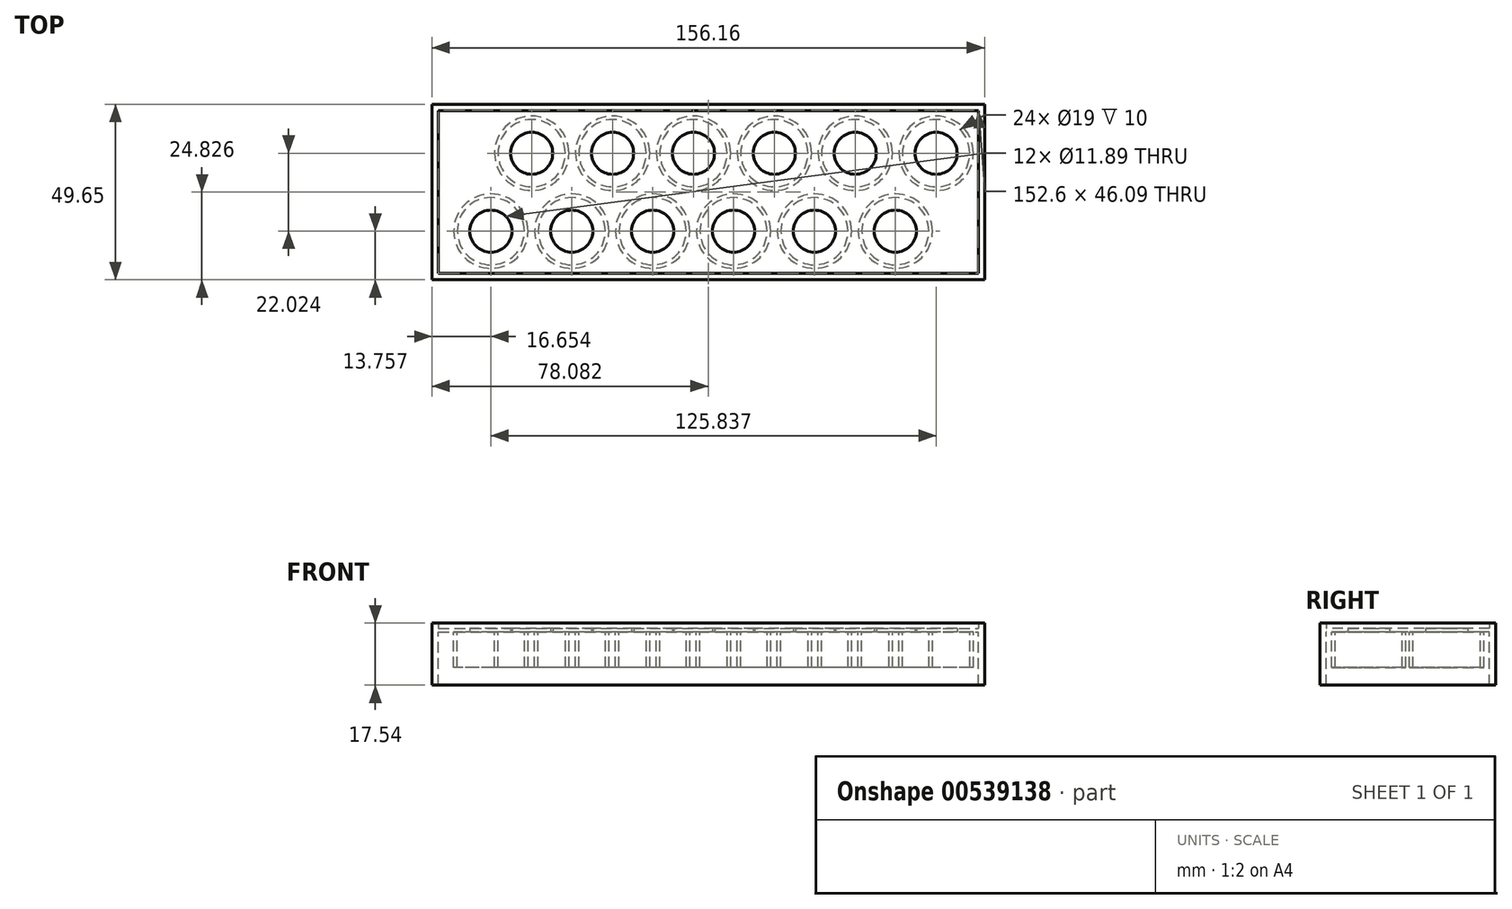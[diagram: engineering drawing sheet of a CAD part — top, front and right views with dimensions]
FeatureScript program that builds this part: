
annotation { "Feature Type Name" : "Feature", "Feature Type Description" : "" }
export const myFeature = defineFeature(function(context is Context, id is Id, definition is map)
    precondition{}
    {
        {
            var Q0;
            Q0=qCreatedBy(makeId("Top.planeOp"),FACE);
            var sketch = newSketch(context, id + "F0", { "sketchPlane" : qUnion([Q0])});
            skCircle(sketch, "E0", {"center": v(-57.63, 20.67) * mm, "radius": 9.5 * mm});
            skCircle(sketch, "E1.0", {"center": v(-57.63, 20.67) * mm, "radius": 10.52 * mm});
            skCircle(sketch, "E2.0.1.0", {"center": v(-46.09, 42.7) * mm, "radius": 10.52 * mm});
            skCircle(sketch, "E2.0.1.1", {"center": v(-46.09, 42.7) * mm, "radius": 9.5 * mm});
            skCircle(sketch, "E2.1.0.0", {"center": v(-34.77, 20.67) * mm, "radius": 10.52 * mm});
            skCircle(sketch, "E2.1.0.1", {"center": v(-34.77, 20.67) * mm, "radius": 9.5 * mm});
            skCircle(sketch, "E2.1.1.0", {"center": v(-23.23, 42.7) * mm, "radius": 10.52 * mm});
            skCircle(sketch, "E2.1.1.1", {"center": v(-23.23, 42.7) * mm, "radius": 9.5 * mm});
            skCircle(sketch, "E2.2.0.0", {"center": v(-11.9, 20.67) * mm, "radius": 10.52 * mm});
            skCircle(sketch, "E2.2.0.1", {"center": v(-11.9, 20.67) * mm, "radius": 9.5 * mm});
            skCircle(sketch, "E2.2.1.0", {"center": v(-0.37, 42.7) * mm, "radius": 10.52 * mm});
            skCircle(sketch, "E2.2.1.1", {"center": v(-0.37, 42.7) * mm, "radius": 9.5 * mm});
            skCircle(sketch, "E2.3.0.0", {"center": v(10.95, 20.67) * mm, "radius": 10.52 * mm});
            skCircle(sketch, "E2.3.0.1", {"center": v(10.95, 20.67) * mm, "radius": 9.5 * mm});
            skCircle(sketch, "E2.3.1.0", {"center": v(22.5, 42.7) * mm, "radius": 10.52 * mm});
            skCircle(sketch, "E2.3.1.1", {"center": v(22.5, 42.7) * mm, "radius": 9.5 * mm});
            skCircle(sketch, "E2.4.0.0", {"center": v(33.81, 20.67) * mm, "radius": 10.52 * mm});
            skCircle(sketch, "E2.4.0.1", {"center": v(33.81, 20.67) * mm, "radius": 9.5 * mm});
            skCircle(sketch, "E2.4.1.0", {"center": v(45.35, 42.7) * mm, "radius": 10.52 * mm});
            skCircle(sketch, "E2.4.1.1", {"center": v(45.35, 42.7) * mm, "radius": 9.5 * mm});
            skCircle(sketch, "E2.5.0.0", {"center": v(56.67, 20.67) * mm, "radius": 10.52 * mm});
            skCircle(sketch, "E2.5.0.1", {"center": v(56.67, 20.67) * mm, "radius": 9.5 * mm});
            skCircle(sketch, "E2.5.1.0", {"center": v(68.21, 42.7) * mm, "radius": 10.52 * mm});
            skCircle(sketch, "E2.5.1.1", {"center": v(68.21, 42.7) * mm, "radius": 9.5 * mm});
            skLineSegment(sketch, "E2.direction1", {"start": v(-57.63, 20.67) * mm, "end": v(-34.77, 20.67) * mm, "construction": true});
            skLineSegment(sketch, "E2.direction2", {"start": v(-57.63, 20.67) * mm, "end": v(-46.09, 42.7) * mm, "construction": true});
            skLineSegment(sketch, "E3.bottom", {"start": v(-74.28, 56.56) * mm, "end": v(81.88, 56.56) * mm});
            skLineSegment(sketch, "E3.top", {"start": v(-74.28, 6.91) * mm, "end": v(81.88, 6.91) * mm});
            skLineSegment(sketch, "E3.left", {"start": v(-74.28, 56.56) * mm, "end": v(-74.28, 6.91) * mm});
            skLineSegment(sketch, "E3.right", {"start": v(81.88, 56.56) * mm, "end": v(81.88, 6.91) * mm});
            skLineSegment(sketch, "E4.0", {"start": v(-72.5, 54.78) * mm, "end": v(80.1, 54.78) * mm});
            skLineSegment(sketch, "E4.1", {"start": v(-72.5, 54.78) * mm, "end": v(-72.5, 8.7) * mm});
            skLineSegment(sketch, "E4.2", {"start": v(-72.5, 8.7) * mm, "end": v(80.1, 8.7) * mm});
            skLineSegment(sketch, "E4.3", {"start": v(80.1, 54.78) * mm, "end": v(80.1, 8.7) * mm});
            skCircle(sketch, "E5.0", {"center": v(-57.63, 20.67) * mm, "radius": 5.94 * mm});
            skCircle(sketch, "E6.0", {"center": v(-46.09, 42.7) * mm, "radius": 5.94 * mm});
            skCircle(sketch, "E7.0", {"center": v(-23.23, 42.7) * mm, "radius": 5.94 * mm});
            skCircle(sketch, "E8.0", {"center": v(-34.77, 20.67) * mm, "radius": 5.94 * mm});
            skCircle(sketch, "E9.0", {"center": v(-0.37, 42.7) * mm, "radius": 5.94 * mm});
            skCircle(sketch, "E10.0", {"center": v(-11.9, 20.67) * mm, "radius": 5.94 * mm});
            skCircle(sketch, "E11.0", {"center": v(10.95, 20.67) * mm, "radius": 5.94 * mm});
            skCircle(sketch, "E12.0", {"center": v(22.5, 42.7) * mm, "radius": 5.94 * mm});
            skCircle(sketch, "E13.0", {"center": v(33.81, 20.67) * mm, "radius": 5.94 * mm});
            skCircle(sketch, "E14.0", {"center": v(45.35, 42.7) * mm, "radius": 5.94 * mm});
            skCircle(sketch, "E15.0", {"center": v(56.67, 20.67) * mm, "radius": 5.94 * mm});
            skCircle(sketch, "E16.0", {"center": v(68.21, 42.7) * mm, "radius": 5.94 * mm});
            skSolve(sketch);
        }
        {
            var Q0;
            Q0=makeQuery(id+"F0.imprint","IMPRINT",FACE,{"disambiguationData":[TD([[makeQuery(id+"F0.imprint","IMPRINT",EDGE,{"derivedFrom":sQuery(id+"F0.wireOp",EDGE,"E3.bottom")}),-1.0]])]});
            extrude(context, id + "F1", {"entities" : qUnion([Q0]), "depth" : 2.54 * mm, "offsetDistance" : 25.4 * mm});
        }
        {
            var Q0;
            Q0=makeQuery(id+"F0.imprint","IMPRINT",FACE,{"disambiguationData":[TD([[makeQuery(id+"F0.imprint","IMPRINT",EDGE,{"derivedFrom":sQuery(id+"F0.wireOp",EDGE,"E2.0.1.0")}),1.0]])]});
            var Q1;
            Q1=makeQuery(id+"F0.imprint","IMPRINT",FACE,{"disambiguationData":[TD([[makeQuery(id+"F0.imprint","IMPRINT",EDGE,{"derivedFrom":sQuery(id+"F0.wireOp",EDGE,"E0")}),-1.0]])]});
            var Q2;
            Q2=makeQuery(id+"F0.imprint","IMPRINT",FACE,{"disambiguationData":[TD([[makeQuery(id+"F0.imprint","IMPRINT",EDGE,{"derivedFrom":sQuery(id+"F0.wireOp",EDGE,"E2.1.0.0")}),1.0]])]});
            var Q3;
            Q3=makeQuery(id+"F0.imprint","IMPRINT",FACE,{"disambiguationData":[TD([[makeQuery(id+"F0.imprint","IMPRINT",EDGE,{"derivedFrom":sQuery(id+"F0.wireOp",EDGE,"E2.1.1.0")}),1.0]])]});
            var Q4;
            Q4=makeQuery(id+"F0.imprint","IMPRINT",FACE,{"disambiguationData":[TD([[makeQuery(id+"F0.imprint","IMPRINT",EDGE,{"derivedFrom":sQuery(id+"F0.wireOp",EDGE,"E2.2.1.0")}),1.0]])]});
            var Q5;
            Q5=makeQuery(id+"F0.imprint","IMPRINT",FACE,{"disambiguationData":[TD([[makeQuery(id+"F0.imprint","IMPRINT",EDGE,{"derivedFrom":sQuery(id+"F0.wireOp",EDGE,"E2.2.0.0")}),1.0]])]});
            var Q6;
            Q6=makeQuery(id+"F0.imprint","IMPRINT",FACE,{"disambiguationData":[TD([[makeQuery(id+"F0.imprint","IMPRINT",EDGE,{"derivedFrom":sQuery(id+"F0.wireOp",EDGE,"E2.3.0.0")}),1.0]])]});
            var Q7;
            Q7=makeQuery(id+"F0.imprint","IMPRINT",FACE,{"disambiguationData":[TD([[makeQuery(id+"F0.imprint","IMPRINT",EDGE,{"derivedFrom":sQuery(id+"F0.wireOp",EDGE,"E2.3.1.0")}),1.0]])]});
            var Q8;
            Q8=makeQuery(id+"F0.imprint","IMPRINT",FACE,{"disambiguationData":[TD([[makeQuery(id+"F0.imprint","IMPRINT",EDGE,{"derivedFrom":sQuery(id+"F0.wireOp",EDGE,"E2.4.0.0")}),1.0]])]});
            var Q9;
            Q9=makeQuery(id+"F0.imprint","IMPRINT",FACE,{"disambiguationData":[TD([[makeQuery(id+"F0.imprint","IMPRINT",EDGE,{"derivedFrom":sQuery(id+"F0.wireOp",EDGE,"E2.4.1.0")}),1.0]])]});
            var Q10;
            Q10=makeQuery(id+"F0.imprint","IMPRINT",FACE,{"disambiguationData":[TD([[makeQuery(id+"F0.imprint","IMPRINT",EDGE,{"derivedFrom":sQuery(id+"F0.wireOp",EDGE,"E2.5.0.0")}),1.0]])]});
            var Q11;
            Q11=makeQuery(id+"F0.imprint","IMPRINT",FACE,{"disambiguationData":[TD([[makeQuery(id+"F0.imprint","IMPRINT",EDGE,{"derivedFrom":sQuery(id+"F0.wireOp",EDGE,"E2.5.1.0")}),1.0]])]});
            extrude(context, id + "F2", {"entities" : qUnion([Q0, Q1, Q2, Q3, Q4, Q5, Q6, Q7, Q8, Q9, Q10, Q11]), "depth" : -10 * mm, "offsetDistance" : 25.4 * mm});
        }
        {
            var Q0;
            Q0=makeQuery(id+"F0.imprint","IMPRINT",FACE,{"disambiguationData":[TD([[makeQuery(id+"F0.imprint","IMPRINT",EDGE,{"derivedFrom":sQuery(id+"F0.wireOp",EDGE,"E1.0")}),-1.0]])]});
            var Q1;
            Q1=makeQuery(id+"F0.imprint","IMPRINT",FACE,{"disambiguationData":[TD([[makeQuery(id+"F0.imprint","IMPRINT",EDGE,{"derivedFrom":sQuery(id+"F0.wireOp",EDGE,"E2.0.1.1")}),1.0]])]});
            var Q2;
            Q2=makeQuery(id+"F0.imprint","IMPRINT",FACE,{"disambiguationData":[TD([[makeQuery(id+"F0.imprint","IMPRINT",EDGE,{"derivedFrom":sQuery(id+"F0.wireOp",EDGE,"E2.1.1.1")}),1.0]])]});
            var Q3;
            Q3=makeQuery(id+"F0.imprint","IMPRINT",FACE,{"disambiguationData":[TD([[makeQuery(id+"F0.imprint","IMPRINT",EDGE,{"derivedFrom":sQuery(id+"F0.wireOp",EDGE,"E0")}),1.0]])]});
            var Q4;
            Q4=makeQuery(id+"F0.imprint","IMPRINT",FACE,{"disambiguationData":[TD([[makeQuery(id+"F0.imprint","IMPRINT",EDGE,{"derivedFrom":sQuery(id+"F0.wireOp",EDGE,"E2.1.0.1")}),1.0]])]});
            var Q5;
            Q5=makeQuery(id+"F0.imprint","IMPRINT",FACE,{"disambiguationData":[TD([[makeQuery(id+"F0.imprint","IMPRINT",EDGE,{"derivedFrom":sQuery(id+"F0.wireOp",EDGE,"E2.2.0.1")}),1.0]])]});
            var Q6;
            Q6=makeQuery(id+"F0.imprint","IMPRINT",FACE,{"disambiguationData":[TD([[makeQuery(id+"F0.imprint","IMPRINT",EDGE,{"derivedFrom":sQuery(id+"F0.wireOp",EDGE,"E2.2.1.1")}),1.0]])]});
            var Q7;
            Q7=makeQuery(id+"F0.imprint","IMPRINT",FACE,{"disambiguationData":[TD([[makeQuery(id+"F0.imprint","IMPRINT",EDGE,{"derivedFrom":sQuery(id+"F0.wireOp",EDGE,"E2.3.1.1")}),1.0]])]});
            var Q8;
            Q8=makeQuery(id+"F0.imprint","IMPRINT",FACE,{"disambiguationData":[TD([[makeQuery(id+"F0.imprint","IMPRINT",EDGE,{"derivedFrom":sQuery(id+"F0.wireOp",EDGE,"E2.3.0.1")}),1.0]])]});
            var Q9;
            Q9=makeQuery(id+"F0.imprint","IMPRINT",FACE,{"disambiguationData":[TD([[makeQuery(id+"F0.imprint","IMPRINT",EDGE,{"derivedFrom":sQuery(id+"F0.wireOp",EDGE,"E2.4.0.1")}),1.0]])]});
            var Q10;
            Q10=makeQuery(id+"F0.imprint","IMPRINT",FACE,{"disambiguationData":[TD([[makeQuery(id+"F0.imprint","IMPRINT",EDGE,{"derivedFrom":sQuery(id+"F0.wireOp",EDGE,"E2.4.1.1")}),1.0]])]});
            var Q11;
            Q11=makeQuery(id+"F0.imprint","IMPRINT",FACE,{"disambiguationData":[TD([[makeQuery(id+"F0.imprint","IMPRINT",EDGE,{"derivedFrom":sQuery(id+"F0.wireOp",EDGE,"E2.5.0.1")}),1.0]])]});
            var Q12;
            Q12=makeQuery(id+"F0.imprint","IMPRINT",FACE,{"disambiguationData":[TD([[makeQuery(id+"F0.imprint","IMPRINT",EDGE,{"derivedFrom":sQuery(id+"F0.wireOp",EDGE,"E2.5.1.1")}),1.0]])]});
            var Q13;
            Q13=makeQuery(id+"F0.imprint","IMPRINT",FACE,{"disambiguationData":[TD([[makeQuery(id+"F0.imprint","IMPRINT",EDGE,{"derivedFrom":sQuery(id+"F0.wireOp",EDGE,"E2.0.1.0")}),1.0]])]});
            var Q14;
            Q14=makeQuery(id+"F0.imprint","IMPRINT",FACE,{"disambiguationData":[TD([[makeQuery(id+"F0.imprint","IMPRINT",EDGE,{"derivedFrom":sQuery(id+"F0.wireOp",EDGE,"E0")}),-1.0]])]});
            var Q15;
            Q15=makeQuery(id+"F0.imprint","IMPRINT",FACE,{"disambiguationData":[TD([[makeQuery(id+"F0.imprint","IMPRINT",EDGE,{"derivedFrom":sQuery(id+"F0.wireOp",EDGE,"E2.1.0.0")}),1.0]])]});
            var Q16;
            Q16=makeQuery(id+"F0.imprint","IMPRINT",FACE,{"disambiguationData":[TD([[makeQuery(id+"F0.imprint","IMPRINT",EDGE,{"derivedFrom":sQuery(id+"F0.wireOp",EDGE,"E2.1.1.0")}),1.0]])]});
            var Q17;
            Q17=makeQuery(id+"F0.imprint","IMPRINT",FACE,{"disambiguationData":[TD([[makeQuery(id+"F0.imprint","IMPRINT",EDGE,{"derivedFrom":sQuery(id+"F0.wireOp",EDGE,"E2.2.1.0")}),1.0]])]});
            var Q18;
            Q18=makeQuery(id+"F0.imprint","IMPRINT",FACE,{"disambiguationData":[TD([[makeQuery(id+"F0.imprint","IMPRINT",EDGE,{"derivedFrom":sQuery(id+"F0.wireOp",EDGE,"E2.3.0.0")}),1.0]])]});
            var Q19;
            Q19=makeQuery(id+"F0.imprint","IMPRINT",FACE,{"disambiguationData":[TD([[makeQuery(id+"F0.imprint","IMPRINT",EDGE,{"derivedFrom":sQuery(id+"F0.wireOp",EDGE,"E2.2.0.0")}),1.0]])]});
            var Q20;
            Q20=makeQuery(id+"F0.imprint","IMPRINT",FACE,{"disambiguationData":[TD([[makeQuery(id+"F0.imprint","IMPRINT",EDGE,{"derivedFrom":sQuery(id+"F0.wireOp",EDGE,"E2.5.0.0")}),1.0]])]});
            var Q21;
            Q21=makeQuery(id+"F0.imprint","IMPRINT",FACE,{"disambiguationData":[TD([[makeQuery(id+"F0.imprint","IMPRINT",EDGE,{"derivedFrom":sQuery(id+"F0.wireOp",EDGE,"E2.4.1.0")}),1.0]])]});
            var Q22;
            Q22=makeQuery(id+"F0.imprint","IMPRINT",FACE,{"disambiguationData":[TD([[makeQuery(id+"F0.imprint","IMPRINT",EDGE,{"derivedFrom":sQuery(id+"F0.wireOp",EDGE,"E2.3.1.0")}),1.0]])]});
            var Q23;
            Q23=makeQuery(id+"F0.imprint","IMPRINT",FACE,{"disambiguationData":[TD([[makeQuery(id+"F0.imprint","IMPRINT",EDGE,{"derivedFrom":sQuery(id+"F0.wireOp",EDGE,"E2.4.0.0")}),1.0]])]});
            var Q24;
            Q24=makeQuery(id+"F0.imprint","IMPRINT",FACE,{"disambiguationData":[TD([[makeQuery(id+"F0.imprint","IMPRINT",EDGE,{"derivedFrom":sQuery(id+"F0.wireOp",EDGE,"E2.5.1.0")}),1.0]])]});
            extrude(context, id + "F3", {"entities" : qUnion([Q0, Q1, Q2, Q3, Q4, Q5, Q6, Q7, Q8, Q9, Q10, Q11, Q12, Q13, Q14, Q15, Q16, Q17, Q18, Q19, Q20, Q21, Q22, Q23, Q24]), "depth" : 1 * mm, "offsetDistance" : 25.4 * mm});
        }
        {
            var Q0;
            Q0=makeQuery(id+"F0.imprint","IMPRINT",FACE,{"disambiguationData":[TD([[makeQuery(id+"F0.imprint","IMPRINT",EDGE,{"derivedFrom":sQuery(id+"F0.wireOp",EDGE,"E3.bottom")}),-1.0]])]});
            extrude(context, id + "F4", {"entities" : qUnion([Q0]), "operationType" : NewBodyOperationType.ADD, "depth" : -15 * mm, "offsetDistance" : 25.4 * mm});
        }
    });
